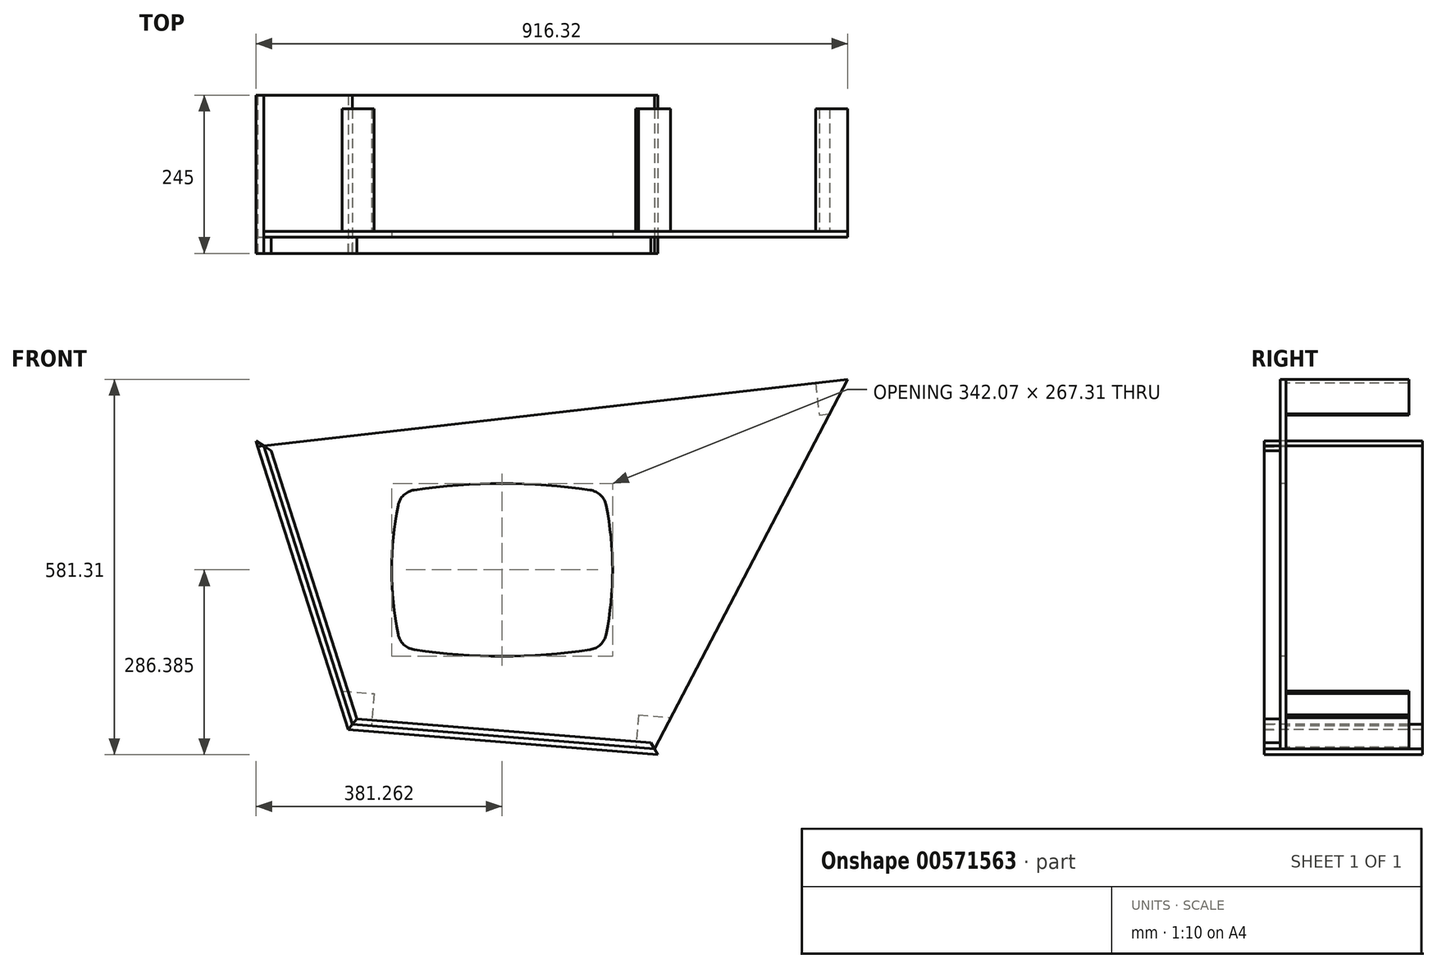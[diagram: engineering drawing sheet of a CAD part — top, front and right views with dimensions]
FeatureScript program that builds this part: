
annotation { "Feature Type Name" : "Feature", "Feature Type Description" : "" }
export const myFeature = defineFeature(function(context is Context, id is Id, definition is map)
    precondition{}
    {
        {
            var Q0;
            Q0=qCreatedBy(makeId("Front.planeOp"),FACE);
            var sketch = newSketch(context, id + "F0", { "sketchPlane" : qUnion([Q0])});
            skLineSegment(sketch, "E0", {"start": v(-464.1, -165.6) * mm, "end": v(3.42, -203.42) * mm});
            skLineSegment(sketch, "E1", {"start": v(3.42, -203.42) * mm, "end": v(302.65, 368.44) * mm});
            skLineSegment(sketch, "E2", {"start": v(-464.1, -165.6) * mm, "end": v(-601.77, 265.5) * mm});
            skLineSegment(sketch, "E3", {"start": v(-601.77, 265.5) * mm, "end": v(302.65, 368.44) * mm});
            skLineSegment(sketch, "E4", {"start": v(-321.91, -100.8) * mm, "end": v(-150, -100.8) * mm, "construction": true});
            skLineSegment(sketch, "E5", {"start": v(-382.41, -121.82) * mm, "end": v(-83.18, -121.82) * mm, "construction": true});
            skPoint(sketch, "E6", {"position": v(-346.5, -121.82) * mm});
            skPoint(sketch, "E7", {"position": v(-112.56, -121.82) * mm});
            skPoint(sketch, "E8", {"position": v(-388.98, 193.86) * mm});
            skPoint(sketch, "E9", {"position": v(-75.84, -46.83) * mm});
            skLineSegment(sketch, "E10", {"start": v(-388.98, 193.86) * mm, "end": v(-75.84, -46.83) * mm, "construction": true});
            skLineSegment(sketch, "E11", {"start": v(302, 428.92) * mm, "end": v(302.65, 368.44) * mm, "construction": true});
            skLineSegment(sketch, "E12", {"start": v(-601.77, 265.5) * mm, "end": v(-603.44, 419.07) * mm, "construction": true});
            skLineSegment(sketch, "E13", {"start": v(-464.1, -165.6) * mm, "end": v(-463.06, -260.6) * mm, "construction": true});
            skLineSegment(sketch, "E14", {"start": v(-464.1, -165.6) * mm, "end": v(-656.09, -167.7) * mm, "construction": true});
            skLineSegment(sketch, "E15", {"start": v(-655.05, -262.7) * mm, "end": v(-23.84, -472.38) * mm});
            skSolve(sketch);
        }
        {
            var Q0;
            Q0=qCreatedBy(makeId("Front.planeOp"),FACE);
            var sketch = newSketch(context, id + "F1", { "sketchPlane" : qUnion([Q0])});
            skLineSegment(sketch, "E16.0", {"start": v(-464.1, -165.6) * mm, "end": v(-601.77, 265.5) * mm});
            skLineSegment(sketch, "E16.1", {"start": v(-1049.97, 214.5) * mm, "end": v(-601.77, 265.5) * mm, "construction": true});
            skLineSegment(sketch, "E16.2", {"start": v(3.42, -203.42) * mm, "end": v(302.65, 368.44) * mm});
            skLineSegment(sketch, "E16.3", {"start": v(-464.1, -165.6) * mm, "end": v(3.42, -203.42) * mm});
            skPoint(sketch, "E17.0", {"position": v(-346.5, -121.82) * mm});
            skLineSegment(sketch, "E17.1", {"start": v(-382.41, -121.82) * mm, "end": v(-83.18, -121.82) * mm});
            skPoint(sketch, "E17.2", {"position": v(-112.56, -121.82) * mm});
            skLineSegment(sketch, "E18.bottom", {"start": v(-388.98, 193.86) * mm, "end": v(-75.84, 193.86) * mm, "construction": true});
            skLineSegment(sketch, "E18.top", {"start": v(-388.98, -46.83) * mm, "end": v(-75.84, -46.83) * mm, "construction": true});
            skLineSegment(sketch, "E18.left", {"start": v(-388.98, 193.86) * mm, "end": v(-388.98, -46.83) * mm, "construction": true});
            skLineSegment(sketch, "E18.right", {"start": v(-75.84, 193.86) * mm, "end": v(-75.84, -46.83) * mm, "construction": true});
            skLineSegment(sketch, "E19", {"start": v(-346.5, -121.82) * mm, "end": v(-112.56, -121.82) * mm, "construction": true});
            skLineSegment(sketch, "E20", {"start": v(-232.4, -121.82) * mm, "end": v(-232.4, 196.57) * mm, "construction": true});
            skPoint(sketch, "E21", {"position": v(-232.4, -46.83) * mm});
            skArc(sketch, "E22", {"start": v(-71.28, -26.32) * mm, "mid": v(-61.37, 73.52) * mm, "end": v(-71.28, 173.35) * mm});
            skArc(sketch, "E23", {"start": v(-368.52, -50.1) * mm, "mid": v(-232.4, -60.14) * mm, "end": v(-96.3, -50.1) * mm});
            skLineSegment(sketch, "E24", {"start": v(-388.98, 73.52) * mm, "end": v(-75.84, 73.52) * mm, "construction": true});
            skArc(sketch, "E25.MirrorCS", {"start": v(-368.52, 197.13) * mm, "mid": v(-232.4, 207.17) * mm, "end": v(-96.3, 197.13) * mm});
            skArc(sketch, "E26.MirrorCS", {"start": v(-393.53, -26.32) * mm, "mid": v(-403.44, 73.52) * mm, "end": v(-393.53, 173.35) * mm});
            skPoint(sketch, "E27.visualSharp", {"position": v(-75.84, 193.86) * mm});
            skArc(sketch, "E27.filletArc", {"start": v(-71.28, 173.35) * mm, "mid": v(-80.03, 189.2) * mm, "end": v(-96.3, 197.13) * mm});
            skPoint(sketch, "E28.visualSharp", {"position": v(-75.84, -46.83) * mm});
            skArc(sketch, "E28.filletArc", {"start": v(-96.3, -50.1) * mm, "mid": v(-80.03, -42.16) * mm, "end": v(-71.28, -26.32) * mm});
            skPoint(sketch, "E29.visualSharp", {"position": v(-388.98, -46.83) * mm});
            skArc(sketch, "E29.filletArc", {"start": v(-393.53, -26.32) * mm, "mid": v(-384.8, -42.16) * mm, "end": v(-368.52, -50.1) * mm});
            skPoint(sketch, "E30.visualSharp", {"position": v(-388.98, 193.86) * mm});
            skArc(sketch, "E30.filletArc", {"start": v(-368.52, 197.13) * mm, "mid": v(-384.8, 189.2) * mm, "end": v(-393.53, 173.35) * mm});
            skPoint(sketch, "E31.orphan", {"position": v(-601.77, 265.5) * mm});
            skLineSegment(sketch, "E32", {"start": v(-601.77, 265.5) * mm, "end": v(302.65, 368.44) * mm});
            skSolve(sketch);
        }
        {
            var Q0;
            Q0=makeQuery(id+"F1.imprint","IMPRINT",FACE,{"disambiguationData":[TD([[makeQuery(id+"F1.imprint","IMPRINT",EDGE,{"derivedFrom":sQuery(id+"F1.wireOp",EDGE,"E16.0")}),-1.0]])]});
            extrude(context, id + "F2", {"entities" : qUnion([Q0]), "oppositeDirection" : true, "depth" : 9 * mm, "offsetDistance" : 25 * mm});
        }
        {
            var Q0;
            Q0=qCreatedBy(makeId("Front.planeOp"),FACE);
            var sketch = newSketch(context, id + "F3", { "sketchPlane" : qUnion([Q0])});
            skLineSegment(sketch, "E33.0", {"start": v(-464.1, -165.6) * mm, "end": v(3.42, -203.42) * mm});
            skLineSegment(sketch, "E33.1", {"start": v(-464.1, -165.6) * mm, "end": v(-601.77, 265.5) * mm});
            skLineSegment(sketch, "E33.2", {"start": v(-1049.97, 214.5) * mm, "end": v(-601.77, 265.5) * mm});
            skLineSegment(sketch, "E33.3", {"start": v(3.42, -203.42) * mm, "end": v(302.65, 368.44) * mm});
            skLineSegment(sketch, "E34.0", {"start": v(8.63, -212.87) * mm, "end": v(318.5, 379.3) * mm});
            skLineSegment(sketch, "E35.0", {"start": v(-613.67, 273.2) * mm, "end": v(318.5, 379.3) * mm});
            skLineSegment(sketch, "E36.0", {"start": v(-470.84, -174.1) * mm, "end": v(-613.67, 273.2) * mm});
            skLineSegment(sketch, "E37.0", {"start": v(-470.84, -174.1) * mm, "end": v(8.63, -212.87) * mm});
            skLineSegment(sketch, "E38", {"start": v(318.5, 379.3) * mm, "end": v(-601.77, 265.5) * mm});
            skLineSegment(sketch, "E39", {"start": v(-613.67, 273.2) * mm, "end": v(-601.77, 265.5) * mm});
            skLineSegment(sketch, "E40", {"start": v(-470.84, -174.1) * mm, "end": v(-464.1, -165.6) * mm});
            skLineSegment(sketch, "E41", {"start": v(3.42, -203.42) * mm, "end": v(8.63, -212.87) * mm});
            skLineSegment(sketch, "E42.0", {"start": v(-457.36, -157.12) * mm, "end": v(-1.8, -193.97) * mm});
            skLineSegment(sketch, "E43.0", {"start": v(-457.36, -157.12) * mm, "end": v(-589.86, 257.8) * mm});
            skLineSegment(sketch, "E44.0", {"start": v(-1.8, -193.97) * mm, "end": v(286.81, 357.58) * mm});
            skLineSegment(sketch, "E45", {"start": v(-464.1, -165.6) * mm, "end": v(-457.36, -157.12) * mm});
            skLineSegment(sketch, "E46", {"start": v(-601.77, 265.5) * mm, "end": v(-589.86, 257.8) * mm});
            skLineSegment(sketch, "E47.trimOffspring", {"start": v(-589.86, 257.8) * mm, "end": v(286.81, 357.58) * mm});
            skLineSegment(sketch, "E48", {"start": v(286.81, 357.58) * mm, "end": v(-601.77, 265.5) * mm});
            skLineSegment(sketch, "E49", {"start": v(-1.8, -193.97) * mm, "end": v(3.42, -203.42) * mm});
            skSolve(sketch);
        }
        {
            var Q0;
            Q0=makeQuery(id+"F3.imprint","IMPRINT",FACE,{"disambiguationData":[TD([[makeQuery(id+"F3.imprint","IMPRINT",EDGE,{"derivedFrom":sQuery(id+"F3.wireOp",EDGE,"E33.0")}),-1.0]])]});
            var Q1;
            Q1=makeQuery(id+"F3.imprint","IMPRINT",FACE,{"disambiguationData":[TD([[makeQuery(id+"F3.imprint","IMPRINT",EDGE,{"derivedFrom":sQuery(id+"F3.wireOp",EDGE,"E33.2")}),1.0]])]});
            var Q2;
            Q2 = qConstructionFilter(qBodyType(qCreatedBy(id + "F3" ,EDGE), BodyType.WIRE), ConstructionObject.NO);
            extrude(context, id + "F4", {"entities" : qUnion([Q0, Q1]), "surfaceEntities" : qUnion([Q2]), "oppositeDirection" : true, "depth" : 220 * mm, "offsetDistance" : 25 * mm, "hasSecondDirection" : true, "secondDirectionOppositeDirection" : false, "secondDirectionDepth" : 25 * mm});
        }
        {
            var Q0;
            Q0=makeQuery(id+"F3.imprint","IMPRINT",FACE,{"disambiguationData":[TD([[makeQuery(id+"F3.imprint","IMPRINT",EDGE,{"derivedFrom":sQuery(id+"F3.wireOp",EDGE,"E33.1")}),1.0]])]});
            var Q1;
            Q1=makeQuery(id+"F3.imprint","IMPRINT",FACE,{"disambiguationData":[TD([[makeQuery(id+"F3.imprint","IMPRINT",EDGE,{"derivedFrom":sQuery(id+"F3.wireOp",EDGE,"E33.3")}),-1.0]])]});
            extrude(context, id + "F5", {"entities" : qUnion([Q0, Q1]), "oppositeDirection" : true, "depth" : 220 * mm, "offsetDistance" : 25 * mm, "hasSecondDirection" : true, "secondDirectionOppositeDirection" : false, "secondDirectionDepth" : 25 * mm});
        }
        {
            var Q0;
            Q0=makeQuery(id+"F3.imprint","IMPRINT",FACE,{"disambiguationData":[TD([[makeQuery(id+"F3.imprint","IMPRINT",EDGE,{"derivedFrom":sQuery(id+"F3.wireOp",EDGE,"E33.1")}),-1.0]])]});
            var Q1;
            Q1=makeQuery(id+"F3.imprint","IMPRINT",FACE,{"disambiguationData":[TD([[makeQuery(id+"F3.imprint","IMPRINT",EDGE,{"derivedFrom":sQuery(id+"F3.wireOp",EDGE,"E33.3")}),1.0]])]});
            extrude(context, id + "F6", {"entities" : qUnion([Q0, Q1]), "depth" : 25 * mm, "offsetDistance" : 25 * mm});
        }
        {
            var Q0;
            Q0=makeQuery(id+"F3.imprint","IMPRINT",FACE,{"disambiguationData":[TD([[makeQuery(id+"F3.imprint","IMPRINT",EDGE,{"derivedFrom":sQuery(id+"F3.wireOp",EDGE,"E33.0")}),1.0]])]});
            var Q1;
            Q1=makeQuery(id+"F3.imprint","IMPRINT",FACE,{"disambiguationData":[TD([[makeQuery(id+"F3.imprint","IMPRINT",EDGE,{"derivedFrom":sQuery(id+"F3.wireOp",EDGE,"E33.2")}),-1.0]])]});
            extrude(context, id + "F7", {"entities" : qUnion([Q0, Q1]), "depth" : 25 * mm, "offsetDistance" : 25 * mm});
        }
        {
            var Q0;
            Q0=qCreatedBy(makeId("Front.planeOp"),FACE);
            var sketch = newSketch(context, id + "F8", { "sketchPlane" : qUnion([Q0])});
            skLineSegment(sketch, "E50.0", {"start": v(-1049.97, 214.5) * mm, "end": v(-601.77, 265.5) * mm});
            skLineSegment(sketch, "E50.1", {"start": v(-464.1, -165.6) * mm, "end": v(-601.77, 265.5) * mm});
            skLineSegment(sketch, "E50.2", {"start": v(3.42, -203.42) * mm, "end": v(302.65, 368.44) * mm});
            skLineSegment(sketch, "E50.3", {"start": v(-464.1, -165.6) * mm, "end": v(3.42, -203.42) * mm});
            skLineSegment(sketch, "E51.bottom", {"start": v(-1049.97, 214.5) * mm, "end": v(-1000.29, 220.15) * mm});
            skLineSegment(sketch, "E51.top", {"start": v(-1044.31, 164.82) * mm, "end": v(-994.63, 170.47) * mm});
            skLineSegment(sketch, "E51.left", {"start": v(-1049.97, 214.5) * mm, "end": v(-1044.31, 164.82) * mm});
            skLineSegment(sketch, "E51.right", {"start": v(-1000.29, 220.15) * mm, "end": v(-994.63, 170.47) * mm});
            skPoint(sketch, "E52", {"position": v(-1049.97, 214.5) * mm});
            skLineSegment(sketch, "E53.bottom", {"start": v(252.97, 362.79) * mm, "end": v(302.65, 368.44) * mm});
            skLineSegment(sketch, "E53.top", {"start": v(258.63, 313.1) * mm, "end": v(308.3, 318.76) * mm});
            skLineSegment(sketch, "E53.left", {"start": v(252.97, 362.79) * mm, "end": v(258.63, 313.1) * mm});
            skLineSegment(sketch, "E53.right", {"start": v(302.65, 368.44) * mm, "end": v(308.3, 318.76) * mm});
            skLineSegment(sketch, "E54.bottom", {"start": v(-21.23, -151.27) * mm, "end": v(28.6, -155.3) * mm});
            skLineSegment(sketch, "E54.top", {"start": v(-25.26, -201.1) * mm, "end": v(24.57, -205.13) * mm});
            skLineSegment(sketch, "E54.left", {"start": v(-21.23, -151.27) * mm, "end": v(-25.26, -201.1) * mm});
            skLineSegment(sketch, "E54.right", {"start": v(28.6, -155.3) * mm, "end": v(24.57, -205.13) * mm});
            skLineSegment(sketch, "E55.bottom", {"start": v(-480.54, -114.11) * mm, "end": v(-430.7, -118.14) * mm});
            skLineSegment(sketch, "E55.top", {"start": v(-484.57, -163.95) * mm, "end": v(-434.73, -167.98) * mm});
            skLineSegment(sketch, "E55.left", {"start": v(-480.54, -114.11) * mm, "end": v(-484.57, -163.95) * mm});
            skLineSegment(sketch, "E55.right", {"start": v(-430.7, -118.14) * mm, "end": v(-434.73, -167.98) * mm});
            skSolve(sketch);
        }
        {
            var Q0;
            Q0=makeQuery(id+"F2.opExtrude","CAP_FACE",FACE,{"disambiguationData":[OSD([sQuery(id+"F1.wireOp",EDGE,"E16.0"),sQuery(id+"F1.wireOp",EDGE,"E16.1"),sQuery(id+"F1.wireOp",EDGE,"E16.2"),sQuery(id+"F1.wireOp",EDGE,"E16.3"),sQuery(id+"F1.wireOp",EDGE,"E22"),sQuery(id+"F1.wireOp",EDGE,"E23"),sQuery(id+"F1.wireOp",EDGE,"E25.MirrorCS"),sQuery(id+"F1.wireOp",EDGE,"E26.MirrorCS"),sQuery(id+"F1.wireOp",EDGE,"E27.filletArc"),sQuery(id+"F1.wireOp",EDGE,"E28.filletArc"),sQuery(id+"F1.wireOp",EDGE,"E29.filletArc"),sQuery(id+"F1.wireOp",EDGE,"E30.filletArc")])],"isStart":false});
            var sketch = newSketch(context, id + "F9", { "sketchPlane" : qUnion([Q0])});
            skLineSegment(sketch, "E56.0", {"start": v(-3.42, -203.42) * mm, "end": v(-302.65, 368.44) * mm});
            skLineSegment(sketch, "E56.1", {"start": v(-258.63, 313.1) * mm, "end": v(-308.3, 318.76) * mm});
            skLineSegment(sketch, "E56.2", {"start": v(-252.97, 362.79) * mm, "end": v(-258.63, 313.1) * mm});
            skLineSegment(sketch, "E56.3", {"start": v(1049.97, 214.5) * mm, "end": v(601.77, 265.5) * mm});
            skLineSegment(sketch, "E57.0", {"start": v(21.23, -151.27) * mm, "end": v(25.26, -201.1) * mm});
            skLineSegment(sketch, "E57.1", {"start": v(464.1, -165.6) * mm, "end": v(-3.42, -203.42) * mm});
            skLineSegment(sketch, "E57.3", {"start": v(21.23, -151.27) * mm, "end": v(-28.6, -155.3) * mm});
            skLineSegment(sketch, "E58.0", {"start": v(430.7, -118.14) * mm, "end": v(434.73, -167.98) * mm});
            skLineSegment(sketch, "E58.1", {"start": v(480.54, -114.11) * mm, "end": v(430.7, -118.14) * mm});
            skLineSegment(sketch, "E58.2", {"start": v(464.1, -165.6) * mm, "end": v(601.77, 265.5) * mm});
            skLineSegment(sketch, "E59.0", {"start": v(1044.31, 164.82) * mm, "end": v(994.63, 170.47) * mm});
            skLineSegment(sketch, "E59.1", {"start": v(1000.29, 220.15) * mm, "end": v(994.63, 170.47) * mm});
            skSolve(sketch);
        }
        {
            var Q0;
            {var subQ5=sQuery(id+"F9.wireOp",EDGE,"E56.2");Q0=makeQuery(id+"F9.imprint","IMPRINT",FACE,{"disambiguationData":[TD([[makeQuery(id+"F9.imprint","IMPRINT",EDGE,{"derivedFrom":subQ5}),-1.0]])]});}
            var Q1;
            {var subQ4=sQuery(id+"F9.wireOp",EDGE,"E57.0");Q1=makeQuery(id+"F9.imprint","IMPRINT",FACE,{"disambiguationData":[TD([[makeQuery(id+"F9.imprint","IMPRINT",EDGE,{"derivedFrom":subQ4}),-1.0]])]});}
            var Q2;
            {var subQ3=sQuery(id+"F9.wireOp",EDGE,"E58.0");Q2=makeQuery(id+"F9.imprint","IMPRINT",FACE,{"disambiguationData":[TD([[makeQuery(id+"F9.imprint","IMPRINT",EDGE,{"derivedFrom":subQ3}),1.0]])]});}
            var Q3;
            {var subQ3=sQuery(id+"F9.wireOp",EDGE,"E59.1");Q3=makeQuery(id+"F9.imprint","IMPRINT",FACE,{"disambiguationData":[TD([[makeQuery(id+"F9.imprint","IMPRINT",EDGE,{"derivedFrom":subQ3}),1.0]])]});}
            extrude(context, id + "F10", {"entities" : qUnion([Q0, Q1, Q2, Q3]), "depth" : 190 * mm, "offsetDistance" : 25 * mm});
        }
    });
